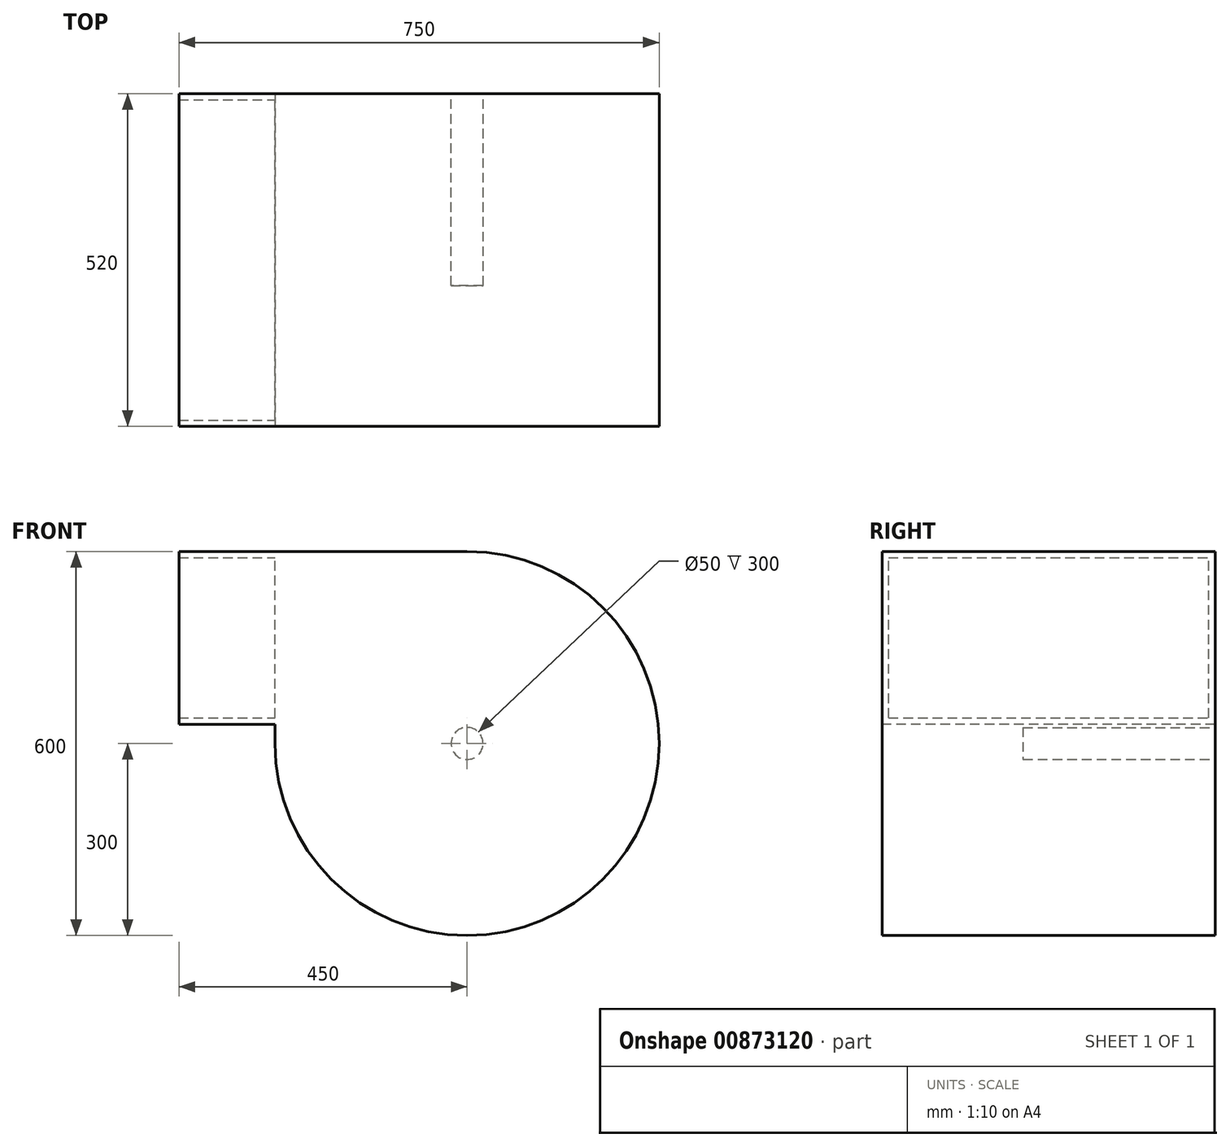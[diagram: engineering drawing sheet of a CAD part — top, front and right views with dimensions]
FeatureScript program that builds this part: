
annotation { "Feature Type Name" : "Feature", "Feature Type Description" : "" }
export const myFeature = defineFeature(function(context is Context, id is Id, definition is map)
    precondition{}
    {
        {
            var Q0;
            Q0=qCreatedBy(makeId("Front.planeOp"),FACE);
            var sketch = newSketch(context, id + "F0", { "sketchPlane" : qUnion([Q0])});
            skLineSegment(sketch, "E0.bottom", {"start": v(300, -300) * mm, "end": v(-300, -300) * mm});
            skLineSegment(sketch, "E0.top", {"start": v(300, 300) * mm, "end": v(-300, 300) * mm});
            skLineSegment(sketch, "E0.left", {"start": v(300, -300) * mm, "end": v(300, 300) * mm});
            skLineSegment(sketch, "E0.right", {"start": v(-300, -300) * mm, "end": v(-300, 300) * mm});
            skPoint(sketch, "E0.middle", {"position": v(0, 0) * mm});
            skSolve(sketch);
        }
        {
            var Q0;
            Q0 = qSketchRegion(id + "F0", true);
            extrude(context, id + "F1", {"entities" : qUnion([Q0]), "depth" : 520 * mm, "offsetDistance" : 25 * mm});
        }
        {
            var Q0;
            Q0=makeQuery(id+"F1.opExtrude","SWEPT_EDGE",EDGE,{"disambiguationData":[OSD([sQuery(id+"F0.wireOp",EDGE,"E0.top"),sQuery(id+"F0.wireOp",EDGE,"E0.left")])]});
            var Q1;
            Q1=makeQuery(id+"F1.opExtrude","SWEPT_EDGE",EDGE,{"disambiguationData":[OSD([sQuery(id+"F0.wireOp",EDGE,"E0.bottom"),sQuery(id+"F0.wireOp",EDGE,"E0.left")])]});
            var Q2;
            Q2=makeQuery(id+"F1.opExtrude","SWEPT_EDGE",EDGE,{"disambiguationData":[OSD([sQuery(id+"F0.wireOp",EDGE,"E0.bottom"),sQuery(id+"F0.wireOp",EDGE,"E0.right")])]});
            fillet(context, id + "F2", {"entities" : qUnion([Q0, Q1, Q2]), "radius" : 300 * mm, "tangentPropagation" : true, "allowEdgeOverflow" : false});
        }
        {
            var Q0;
            Q0=makeQuery(id+"F1.opExtrude","SWEPT_FACE",FACE,{"disambiguationData":[OSD([sQuery(id+"F0.wireOp",EDGE,"E0.right")])]});
            var sketch = newSketch(context, id + "F3", { "sketchPlane" : qUnion([Q0])});
            skLineSegment(sketch, "E1", {"start": v(0, 300) * mm, "end": v(0, 30) * mm});
            skLineSegment(sketch, "E2", {"start": v(0, 30) * mm, "end": v(520, 30) * mm});
            skLineSegment(sketch, "E3", {"start": v(520, 30) * mm, "end": v(520, 300) * mm});
            skLineSegment(sketch, "E4", {"start": v(520, 300) * mm, "end": v(0, 300) * mm});
            skLineSegment(sketch, "E5.bottom", {"start": v(510, 40) * mm, "end": v(10, 40) * mm});
            skLineSegment(sketch, "E5.top", {"start": v(510, 290) * mm, "end": v(10, 290) * mm});
            skLineSegment(sketch, "E5.left", {"start": v(510, 40) * mm, "end": v(510, 290) * mm});
            skLineSegment(sketch, "E5.right", {"start": v(10, 40) * mm, "end": v(10, 290) * mm});
            skPoint(sketch, "E5.middle", {"position": v(260, 165) * mm});
            skPoint(sketch, "E5.middle.positionSnap0", {"position": v(520, 165) * mm});
            skPoint(sketch, "E5.middle.positionSnap1", {"position": v(260, 300) * mm});
            skPoint(sketch, "E5.centerSnap0", {"position": v(520, 165) * mm});
            skPoint(sketch, "E5.centerSnap1", {"position": v(260, 300) * mm});
            skSolve(sketch);
        }
        {
            var Q0;
            Q0 = qSketchRegion(id + "F3", true);
            extrude(context, id + "F4", {"entities" : qUnion([Q0]), "operationType" : NewBodyOperationType.ADD, "depth" : 150 * mm, "offsetDistance" : 25 * mm});
        }
        {
            var Q0;
            Q0=makeQuery(id+"F4.boolean.opBoolean","MERGE",FACE,{"derivedFrom":[makeQuery(id+"F1.opExtrude","CAP_FACE",FACE,{"disambiguationData":[OSD([sQuery(id+"F0.wireOp",EDGE,"E0.bottom"),sQuery(id+"F0.wireOp",EDGE,"E0.top"),sQuery(id+"F0.wireOp",EDGE,"E0.left"),sQuery(id+"F0.wireOp",EDGE,"E0.right")])],"isStart":true}),makeQuery(id+"F4.opExtrude","SWEPT_FACE",FACE,{"disambiguationData":[OSD([sQuery(id+"F3.wireOp",EDGE,"E1")])]})]});
            var sketch = newSketch(context, id + "F5", { "sketchPlane" : qUnion([Q0])});
            skCircle(sketch, "E6", {"center": v(0, 0) * mm, "radius": 25 * mm});
            skSolve(sketch);
        }
        {
            var Q0;
            Q0 = qSketchRegion(id + "F5", true);
            extrude(context, id + "F6", {"entities" : qUnion([Q0]), "operationType" : NewBodyOperationType.REMOVE, "oppositeDirection" : true, "depth" : 300 * mm, "offsetDistance" : 25 * mm});
        }
    });
